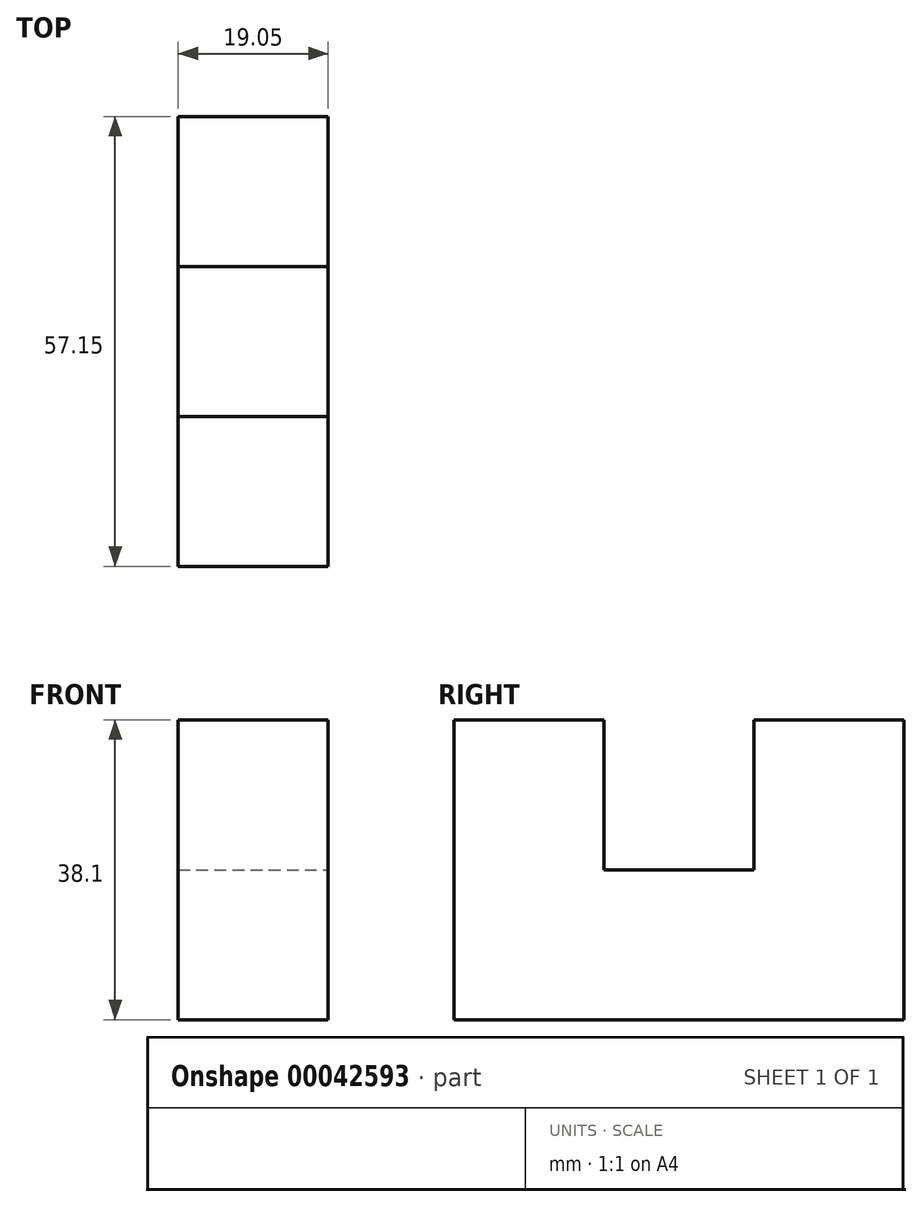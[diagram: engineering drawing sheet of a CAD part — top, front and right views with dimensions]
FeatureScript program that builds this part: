
annotation { "Feature Type Name" : "Feature", "Feature Type Description" : "" }
export const myFeature = defineFeature(function(context is Context, id is Id, definition is map)
    precondition{}
    {
        {
            var Q0;
            Q0=qCreatedBy(makeId("Top.planeOp"),FACE);
            var sketch = newSketch(context, id + "F0", { "sketchPlane" : qUnion([Q0])});
            skLineSegment(sketch, "E0.bottom", {"start": v(-38.37, -39.96) * mm, "end": v(-57.42, -39.96) * mm});
            skLineSegment(sketch, "E0.top", {"start": v(-38.37, 17.19) * mm, "end": v(-57.42, 17.19) * mm});
            skLineSegment(sketch, "E0.left", {"start": v(-38.37, -39.96) * mm, "end": v(-38.37, 17.19) * mm});
            skLineSegment(sketch, "E0.right", {"start": v(-57.42, -39.96) * mm, "end": v(-57.42, 17.19) * mm});
            skSolve(sketch);
        }
        {
            var Q0;
            Q0=makeQuery(id+"F0.imprint","IMPRINT",FACE,{"disambiguationData":[TD([[makeQuery(id+"F0.imprint","IMPRINT",EDGE,{"derivedFrom":sQuery(id+"F0.wireOp",EDGE,"E0.bottom")}),-1.0]])]});
            extrude(context, id + "F1", {"entities" : qUnion([Q0]), "depth" : 19.05 * mm});
        }
        {
            var Q0;
            Q0=makeQuery(id+"F1.opExtrude","CAP_FACE",FACE,{"disambiguationData":[OSD([sQuery(id+"F0.wireOp",EDGE,"E0.bottom"),sQuery(id+"F0.wireOp",EDGE,"E0.top"),sQuery(id+"F0.wireOp",EDGE,"E0.left"),sQuery(id+"F0.wireOp",EDGE,"E0.right")])],"isStart":false});
            var sketch = newSketch(context, id + "F2", { "sketchPlane" : qUnion([Q0])});
            skLineSegment(sketch, "E1.bottom", {"start": v(-57.42, -39.96) * mm, "end": v(-38.37, -39.96) * mm});
            skLineSegment(sketch, "E1.top", {"start": v(-57.42, -20.91) * mm, "end": v(-38.37, -20.91) * mm});
            skLineSegment(sketch, "E1.left", {"start": v(-57.42, -39.96) * mm, "end": v(-57.42, -20.91) * mm});
            skLineSegment(sketch, "E1.right", {"start": v(-38.37, -39.96) * mm, "end": v(-38.37, -20.91) * mm});
            skSolve(sketch);
        }
        {
            var Q0;
            Q0 = qSketchRegion(id + "F2", true);
            extrude(context, id + "F3", {"entities" : qUnion([Q0]), "operationType" : NewBodyOperationType.ADD, "depth" : 19.05 * mm});
        }
        {
            var Q0;
            Q0=makeQuery(id+"F1.opExtrude","CAP_FACE",FACE,{"disambiguationData":[OSD([sQuery(id+"F0.wireOp",EDGE,"E0.bottom"),sQuery(id+"F0.wireOp",EDGE,"E0.top"),sQuery(id+"F0.wireOp",EDGE,"E0.left"),sQuery(id+"F0.wireOp",EDGE,"E0.right")])],"isStart":false});
            var sketch = newSketch(context, id + "F4", { "sketchPlane" : qUnion([Q0])});
            skLineSegment(sketch, "E2.bottom", {"start": v(-57.42, 17.19) * mm, "end": v(-38.37, 17.19) * mm});
            skLineSegment(sketch, "E2.top", {"start": v(-57.42, -1.86) * mm, "end": v(-38.37, -1.86) * mm});
            skLineSegment(sketch, "E2.left", {"start": v(-57.42, 17.19) * mm, "end": v(-57.42, -1.86) * mm});
            skLineSegment(sketch, "E2.right", {"start": v(-38.37, 17.19) * mm, "end": v(-38.37, -1.86) * mm});
            skSolve(sketch);
        }
        {
            var Q0;
            Q0=makeQuery(id+"F4.imprint","IMPRINT",FACE,{"disambiguationData":[TD([[makeQuery(id+"F4.imprint","IMPRINT",EDGE,{"derivedFrom":sQuery(id+"F4.wireOp",EDGE,"E2.bottom")}),1.0]])]});
            extrude(context, id + "F5", {"entities" : qUnion([Q0]), "operationType" : NewBodyOperationType.ADD, "depth" : 19.05 * mm});
        }
    });
